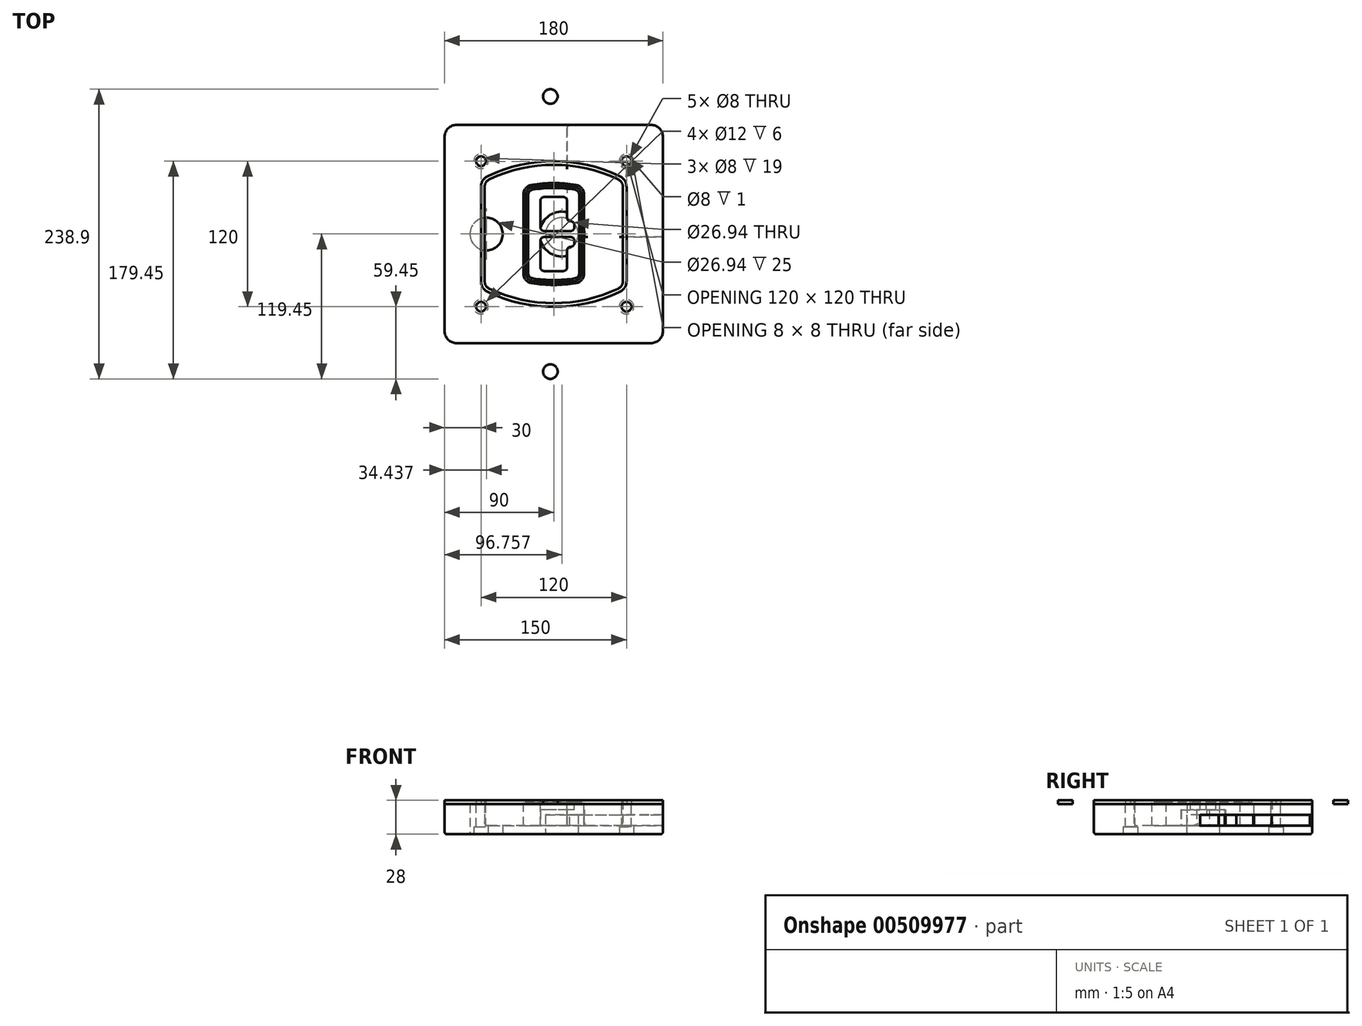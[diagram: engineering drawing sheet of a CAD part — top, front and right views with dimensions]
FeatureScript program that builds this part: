
annotation { "Feature Type Name" : "Feature", "Feature Type Description" : "" }
export const myFeature = defineFeature(function(context is Context, id is Id, definition is map)
    precondition{}
    {
        {
            var Q0;
            Q0=qCreatedBy(makeId("Top.planeOp"),FACE);
            var sketch = newSketch(context, id + "F0", { "sketchPlane" : qUnion([Q0])});
            skPoint(sketch, "E0.rect.middle", {"position": v(0, 0) * mm});
            skLineSegment(sketch, "E1.bottom", {"start": v(-80, -90) * mm, "end": v(80, -90) * mm});
            skLineSegment(sketch, "E1.top", {"start": v(-80, 90) * mm, "end": v(80, 90) * mm});
            skLineSegment(sketch, "E1.left", {"start": v(-90, -80) * mm, "end": v(-90, 80) * mm});
            skLineSegment(sketch, "E1.right", {"start": v(90, -80) * mm, "end": v(90, 80) * mm});
            skLineSegment(sketch, "E2", {"start": v(-90, 90) * mm, "end": v(90, -90) * mm, "construction": true});
            skLineSegment(sketch, "E3", {"start": v(90, 90) * mm, "end": v(-90, -90) * mm, "construction": true});
            skCircle(sketch, "E4", {"center": v(-60, 60) * mm, "radius": 4 * mm});
            skCircle(sketch, "E5", {"center": v(60, 60) * mm, "radius": 4 * mm});
            skCircle(sketch, "E6", {"center": v(60, -60) * mm, "radius": 4 * mm});
            skCircle(sketch, "E7", {"center": v(-60, -60) * mm, "radius": 4 * mm});
            skLineSegment(sketch, "E8", {"start": v(-60, 60) * mm, "end": v(60, 60) * mm, "construction": true});
            skLineSegment(sketch, "E9", {"start": v(60, 60) * mm, "end": v(60, -60) * mm, "construction": true});
            skLineSegment(sketch, "E10", {"start": v(60, -60) * mm, "end": v(-60, -60) * mm, "construction": true});
            skLineSegment(sketch, "E11", {"start": v(-60, -60) * mm, "end": v(-60, 60) * mm, "construction": true});
            skLineSegment(sketch, "E12", {"start": v(-60, 38.83) * mm, "end": v(-60, -38.83) * mm});
            skLineSegment(sketch, "E13", {"start": v(60, 38.83) * mm, "end": v(60, -38.83) * mm});
            skArc(sketch, "E14", {"start": v(54.26, 47.88) * mm, "mid": v(0, 60) * mm, "end": v(-54.26, 47.88) * mm});
            skArc(sketch, "E15", {"start": v(-54.26, -47.88) * mm, "mid": v(0, -60) * mm, "end": v(54.26, -47.88) * mm});
            skLineSegment(sketch, "E16", {"start": v(-60, 0) * mm, "end": v(60, 0) * mm, "construction": true});
            skPoint(sketch, "E17.visualSharp", {"position": v(-60, -45) * mm});
            skArc(sketch, "E17.filletArc", {"start": v(-60, -38.83) * mm, "mid": v(-58.44, -44.2) * mm, "end": v(-54.26, -47.88) * mm});
            skPoint(sketch, "E18.visualSharp", {"position": v(-60, 45) * mm});
            skArc(sketch, "E18.filletArc", {"start": v(-54.26, 47.88) * mm, "mid": v(-58.44, 44.2) * mm, "end": v(-60, 38.83) * mm});
            skPoint(sketch, "E19.visualSharp", {"position": v(60, 45) * mm});
            skArc(sketch, "E19.filletArc", {"start": v(60, 38.83) * mm, "mid": v(58.44, 44.2) * mm, "end": v(54.26, 47.88) * mm});
            skPoint(sketch, "E20.visualSharp", {"position": v(60, -45) * mm});
            skArc(sketch, "E20.filletArc", {"start": v(54.26, -47.88) * mm, "mid": v(58.44, -44.2) * mm, "end": v(60, -38.83) * mm});
            skPoint(sketch, "E21.visualSharp", {"position": v(-90, 90) * mm});
            skArc(sketch, "E21.filletArc", {"start": v(-80, 90) * mm, "mid": v(-87.07, 87.07) * mm, "end": v(-90, 80) * mm});
            skPoint(sketch, "E22.visualSharp", {"position": v(90, 90) * mm});
            skArc(sketch, "E22.filletArc", {"start": v(90, 80) * mm, "mid": v(87.07, 87.07) * mm, "end": v(80, 90) * mm});
            skPoint(sketch, "E23.visualSharp", {"position": v(90, -90) * mm});
            skArc(sketch, "E23.filletArc", {"start": v(80, -90) * mm, "mid": v(87.07, -87.07) * mm, "end": v(90, -80) * mm});
            skPoint(sketch, "E24.visualSharp", {"position": v(-90, -90) * mm});
            skArc(sketch, "E24.filletArc", {"start": v(-90, -80) * mm, "mid": v(-87.07, -87.07) * mm, "end": v(-80, -90) * mm});
            skArc(sketch, "E25.0", {"start": v(57, 38.83) * mm, "mid": v(55.9, 42.58) * mm, "end": v(52.98, 45.17) * mm});
            skLineSegment(sketch, "E25.1", {"start": v(57, 38.83) * mm, "end": v(57, -38.83) * mm});
            skArc(sketch, "E25.2", {"start": v(52.98, -45.17) * mm, "mid": v(55.9, -42.58) * mm, "end": v(57, -38.83) * mm});
            skArc(sketch, "E25.3", {"start": v(-52.98, -45.17) * mm, "mid": v(0, -57) * mm, "end": v(52.98, -45.17) * mm});
            skArc(sketch, "E25.4", {"start": v(-57, -38.83) * mm, "mid": v(-55.9, -42.58) * mm, "end": v(-52.98, -45.17) * mm});
            skArc(sketch, "E25.5", {"start": v(52.98, 45.17) * mm, "mid": v(0, 57) * mm, "end": v(-52.98, 45.17) * mm});
            skLineSegment(sketch, "E25.6", {"start": v(-57, 38.83) * mm, "end": v(-57, -38.83) * mm});
            skArc(sketch, "E25.7", {"start": v(-52.98, 45.17) * mm, "mid": v(-55.9, 42.58) * mm, "end": v(-57, 38.83) * mm});
            skArc(sketch, "E26.0", {"start": v(-55.96, 51.5) * mm, "mid": v(-61.82, 46.33) * mm, "end": v(-64, 38.83) * mm});
            skArc(sketch, "E26.1", {"start": v(55.96, 51.5) * mm, "mid": v(0, 64) * mm, "end": v(-55.96, 51.5) * mm});
            skArc(sketch, "E26.2", {"start": v(64, 38.83) * mm, "mid": v(61.82, 46.33) * mm, "end": v(55.96, 51.5) * mm});
            skLineSegment(sketch, "E26.3", {"start": v(64, 38.83) * mm, "end": v(64, -38.83) * mm});
            skArc(sketch, "E26.4", {"start": v(55.96, -51.5) * mm, "mid": v(61.82, -46.33) * mm, "end": v(64, -38.83) * mm});
            skLineSegment(sketch, "E26.5", {"start": v(-64, 38.83) * mm, "end": v(-64, -38.83) * mm});
            skArc(sketch, "E26.6", {"start": v(-55.96, -51.5) * mm, "mid": v(0, -64) * mm, "end": v(55.96, -51.5) * mm});
            skArc(sketch, "E26.7", {"start": v(-64, -38.83) * mm, "mid": v(-61.82, -46.33) * mm, "end": v(-55.96, -51.5) * mm});
            skSolve(sketch);
        }
        {
            var Q0;
            Q0=makeQuery(id+"F0.imprint","IMPRINT",FACE,{"disambiguationData":[TD([[makeQuery(id+"F0.imprint","IMPRINT",EDGE,{"derivedFrom":sQuery(id+"F0.wireOp",EDGE,"E1.bottom")}),1.0]])]});
            var Q1;
            Q1=makeQuery(id+"F0.imprint","IMPRINT",FACE,{"disambiguationData":[TD([[makeQuery(id+"F0.imprint","IMPRINT",EDGE,{"derivedFrom":sQuery(id+"F0.wireOp",EDGE,"E12")}),1.0]])]});
            var Q2;
            Q2=makeQuery(id+"F0.imprint","IMPRINT",FACE,{"disambiguationData":[TD([[makeQuery(id+"F0.imprint","IMPRINT",EDGE,{"derivedFrom":sQuery(id+"F0.wireOp",EDGE,"E25.0")}),1.0]])]});
            var Q3;
            Q3=makeQuery(id+"F0.imprint","IMPRINT",FACE,{"disambiguationData":[TD([[makeQuery(id+"F0.imprint","IMPRINT",EDGE,{"derivedFrom":sQuery(id+"F0.wireOp",EDGE,"E12")}),-1.0]])]});
            extrude(context, id + "F1", {"entities" : qUnion([Q0, Q1, Q2, Q3]), "oppositeDirection" : true, "depth" : 25 * mm});
        }
        {
            var Q0;
            Q0=makeQuery(id+"F0.imprint","IMPRINT",FACE,{"disambiguationData":[TD([[makeQuery(id+"F0.imprint","IMPRINT",EDGE,{"derivedFrom":sQuery(id+"F0.wireOp",EDGE,"E12")}),1.0]])]});
            extrude(context, id + "F2", {"entities" : qUnion([Q0]), "operationType" : NewBodyOperationType.ADD, "depth" : 3 * mm});
        }
        {
            var Q0;
            Q0=makeQuery(id+"F0.imprint","IMPRINT",FACE,{"disambiguationData":[TD([[makeQuery(id+"F0.imprint","IMPRINT",EDGE,{"derivedFrom":sQuery(id+"F0.wireOp",EDGE,"E25.0")}),1.0]])]});
            extrude(context, id + "F3", {"entities" : qUnion([Q0]), "operationType" : NewBodyOperationType.REMOVE, "oppositeDirection" : true, "depth" : 18 * mm});
        }
        {
            var Q0;
            Q0=makeQuery(id+"F2.opExtrude","CAP_FACE",FACE,{"disambiguationData":[OSD([sQuery(id+"F0.wireOp",EDGE,"E12"),sQuery(id+"F0.wireOp",EDGE,"E13"),sQuery(id+"F0.wireOp",EDGE,"E14"),sQuery(id+"F0.wireOp",EDGE,"E15"),sQuery(id+"F0.wireOp",EDGE,"E17.filletArc"),sQuery(id+"F0.wireOp",EDGE,"E18.filletArc"),sQuery(id+"F0.wireOp",EDGE,"E19.filletArc"),sQuery(id+"F0.wireOp",EDGE,"E20.filletArc"),sQuery(id+"F0.wireOp",EDGE,"E25.0"),sQuery(id+"F0.wireOp",EDGE,"E25.1"),sQuery(id+"F0.wireOp",EDGE,"E25.2"),sQuery(id+"F0.wireOp",EDGE,"E25.3"),sQuery(id+"F0.wireOp",EDGE,"E25.4"),sQuery(id+"F0.wireOp",EDGE,"E25.5"),sQuery(id+"F0.wireOp",EDGE,"E25.6"),sQuery(id+"F0.wireOp",EDGE,"E25.7")])],"isStart":false});
            var sketch = newSketch(context, id + "F4", { "sketchPlane" : qUnion([Q0])});
            skArc(sketch, "E27.0", {"start": v(-18.34, -40.45) * mm, "mid": v(0, -42) * mm, "end": v(18.34, -40.45) * mm});
            skArc(sketch, "E28.0", {"start": v(18.34, 40.45) * mm, "mid": v(0, 42) * mm, "end": v(-18.34, 40.45) * mm});
            skLineSegment(sketch, "E29", {"start": v(-25, 32.57) * mm, "end": v(-25, -32.57) * mm});
            skLineSegment(sketch, "E30", {"start": v(25, 32.57) * mm, "end": v(25, -32.57) * mm});
            skLineSegment(sketch, "E31", {"start": v(-25, 39.1) * mm, "end": v(25, 39.1) * mm, "construction": true});
            skLineSegment(sketch, "E32", {"start": v(-25, -39.1) * mm, "end": v(25, -39.1) * mm, "construction": true});
            skPoint(sketch, "E33.visualSharp", {"position": v(-25, 39.1) * mm});
            skArc(sketch, "E33.filletArc", {"start": v(-18.34, 40.45) * mm, "mid": v(-23.11, 37.73) * mm, "end": v(-25, 32.57) * mm});
            skPoint(sketch, "E34.visualSharp", {"position": v(25, 39.1) * mm});
            skArc(sketch, "E34.filletArc", {"start": v(25, 32.57) * mm, "mid": v(23.11, 37.73) * mm, "end": v(18.34, 40.45) * mm});
            skPoint(sketch, "E35.visualSharp", {"position": v(25, -39.1) * mm});
            skArc(sketch, "E35.filletArc", {"start": v(18.34, -40.45) * mm, "mid": v(23.11, -37.73) * mm, "end": v(25, -32.57) * mm});
            skPoint(sketch, "E36.visualSharp", {"position": v(-25, -39.1) * mm});
            skArc(sketch, "E36.filletArc", {"start": v(-25, -32.57) * mm, "mid": v(-23.11, -37.73) * mm, "end": v(-18.34, -40.45) * mm});
            skArc(sketch, "E37.0", {"start": v(52.98, 45.17) * mm, "mid": v(0, 57) * mm, "end": v(-52.98, 45.17) * mm});
            skArc(sketch, "E37.1", {"start": v(-52.98, 45.17) * mm, "mid": v(-55.9, 42.58) * mm, "end": v(-57, 38.83) * mm});
            skLineSegment(sketch, "E37.2", {"start": v(-57, 38.83) * mm, "end": v(-57, -38.83) * mm});
            skArc(sketch, "E37.3", {"start": v(-57, -38.83) * mm, "mid": v(-55.9, -42.58) * mm, "end": v(-52.98, -45.17) * mm});
            skArc(sketch, "E37.4", {"start": v(-52.98, -45.17) * mm, "mid": v(0, -57) * mm, "end": v(52.98, -45.17) * mm});
            skArc(sketch, "E37.5", {"start": v(52.98, -45.17) * mm, "mid": v(55.9, -42.58) * mm, "end": v(57, -38.83) * mm});
            skLineSegment(sketch, "E37.6", {"start": v(57, 38.83) * mm, "end": v(57, -38.83) * mm});
            skArc(sketch, "E37.7", {"start": v(57, 38.83) * mm, "mid": v(55.9, 42.58) * mm, "end": v(52.98, 45.17) * mm});
            skLineSegment(sketch, "E38.0", {"start": v(23, 32.57) * mm, "end": v(23, -32.57) * mm});
            skArc(sketch, "E38.1", {"start": v(18, -38.48) * mm, "mid": v(21.58, -36.44) * mm, "end": v(23, -32.57) * mm});
            skArc(sketch, "E38.2", {"start": v(-18, -38.48) * mm, "mid": v(0, -40) * mm, "end": v(18, -38.48) * mm});
            skArc(sketch, "E38.3", {"start": v(-23, -32.57) * mm, "mid": v(-21.58, -36.44) * mm, "end": v(-18, -38.48) * mm});
            skLineSegment(sketch, "E38.4", {"start": v(-23, 32.57) * mm, "end": v(-23, -32.57) * mm});
            skArc(sketch, "E38.5", {"start": v(23, 32.57) * mm, "mid": v(21.58, 36.44) * mm, "end": v(18, 38.48) * mm});
            skArc(sketch, "E38.6", {"start": v(-18, 38.48) * mm, "mid": v(-21.58, 36.44) * mm, "end": v(-23, 32.57) * mm});
            skArc(sketch, "E38.7", {"start": v(18, 38.48) * mm, "mid": v(0, 40) * mm, "end": v(-18, 38.48) * mm});
            skArc(sketch, "E39.0", {"start": v(21, 32.57) * mm, "mid": v(20.06, 35.15) * mm, "end": v(17.67, 36.5) * mm});
            skLineSegment(sketch, "E39.1", {"start": v(21, 32.57) * mm, "end": v(21, -32.57) * mm});
            skArc(sketch, "E39.2", {"start": v(17.67, -36.5) * mm, "mid": v(20.06, -35.15) * mm, "end": v(21, -32.57) * mm});
            skArc(sketch, "E39.3", {"start": v(-17.67, -36.5) * mm, "mid": v(0, -38) * mm, "end": v(17.67, -36.5) * mm});
            skArc(sketch, "E39.4", {"start": v(-21, -32.57) * mm, "mid": v(-20.06, -35.15) * mm, "end": v(-17.67, -36.5) * mm});
            skArc(sketch, "E39.5", {"start": v(17.67, 36.5) * mm, "mid": v(0, 38) * mm, "end": v(-17.67, 36.5) * mm});
            skLineSegment(sketch, "E39.6", {"start": v(-21, 32.57) * mm, "end": v(-21, -32.57) * mm});
            skArc(sketch, "E39.7", {"start": v(-17.67, 36.5) * mm, "mid": v(-20.06, 35.15) * mm, "end": v(-21, 32.57) * mm});
            skLineSegment(sketch, "E40", {"start": v(-25, 0) * mm, "end": v(25, 0) * mm, "construction": true});
            skLineSegment(sketch, "E41", {"start": v(-11, 5.5) * mm, "end": v(-11, 27.5) * mm});
            skLineSegment(sketch, "E42", {"start": v(-8, 30.5) * mm, "end": v(8, 30.5) * mm});
            skLineSegment(sketch, "E43", {"start": v(11, 27.5) * mm, "end": v(11, 13.5) * mm});
            skLineSegment(sketch, "E44", {"start": v(14, 10.5) * mm, "end": v(14, 10.5) * mm});
            skLineSegment(sketch, "E45", {"start": v(17, 7.5) * mm, "end": v(17, 5.5) * mm});
            skLineSegment(sketch, "E46", {"start": v(14, 2.5) * mm, "end": v(-8, 2.5) * mm});
            skPoint(sketch, "E47.visualSharp", {"position": v(-11, 30.5) * mm});
            skArc(sketch, "E47.filletArc", {"start": v(-8, 30.5) * mm, "mid": v(-10.12, 29.62) * mm, "end": v(-11, 27.5) * mm});
            skPoint(sketch, "E48.visualSharp", {"position": v(11, 30.5) * mm});
            skArc(sketch, "E48.filletArc", {"start": v(11, 27.5) * mm, "mid": v(10.12, 29.62) * mm, "end": v(8, 30.5) * mm});
            skPoint(sketch, "E49.visualSharp", {"position": v(11, 10.5) * mm});
            skArc(sketch, "E49.filletArc", {"start": v(11, 13.5) * mm, "mid": v(11.88, 11.38) * mm, "end": v(14, 10.5) * mm});
            skPoint(sketch, "E50.visualSharp", {"position": v(17, 10.5) * mm});
            skArc(sketch, "E50.filletArc", {"start": v(17, 7.5) * mm, "mid": v(16.12, 9.62) * mm, "end": v(14, 10.5) * mm});
            skPoint(sketch, "E51.visualSharp", {"position": v(17, 2.5) * mm});
            skArc(sketch, "E51.filletArc", {"start": v(14, 2.5) * mm, "mid": v(16.12, 3.38) * mm, "end": v(17, 5.5) * mm});
            skPoint(sketch, "E52.visualSharp", {"position": v(-11, 2.5) * mm});
            skArc(sketch, "E52.filletArc", {"start": v(-11, 5.5) * mm, "mid": v(-10.12, 3.38) * mm, "end": v(-8, 2.5) * mm});
            skLineSegment(sketch, "E53.0.MirrorCS", {"start": v(14, -2.5) * mm, "end": v(-8, -2.5) * mm});
            skArc(sketch, "E54.0.MirrorCS", {"start": v(-11, -5.5) * mm, "mid": v(-10.12, -3.38) * mm, "end": v(-8, -2.5) * mm});
            skLineSegment(sketch, "E55.0.MirrorCS", {"start": v(-11, -5.5) * mm, "end": v(-11, -27.5) * mm});
            skArc(sketch, "E56.0.MirrorCS", {"start": v(-8, -30.5) * mm, "mid": v(-10.12, -29.62) * mm, "end": v(-11, -27.5) * mm});
            skLineSegment(sketch, "E57.0.MirrorCS", {"start": v(-8, -30.5) * mm, "end": v(8, -30.5) * mm});
            skArc(sketch, "E58.0.MirrorCS", {"start": v(11, -27.5) * mm, "mid": v(10.12, -29.62) * mm, "end": v(8, -30.5) * mm});
            skLineSegment(sketch, "E59.0.MirrorCS", {"start": v(11, -27.5) * mm, "end": v(11, -13.5) * mm});
            skArc(sketch, "E60.0.MirrorCS", {"start": v(11, -13.5) * mm, "mid": v(11.88, -11.38) * mm, "end": v(14, -10.5) * mm});
            skArc(sketch, "E61.0.MirrorCS", {"start": v(17, -7.5) * mm, "mid": v(16.12, -9.62) * mm, "end": v(14, -10.5) * mm});
            skLineSegment(sketch, "E62.0.MirrorCS", {"start": v(17, -7.5) * mm, "end": v(17, -5.5) * mm});
            skArc(sketch, "E63.0.MirrorCS", {"start": v(14, -2.5) * mm, "mid": v(16.12, -3.38) * mm, "end": v(17, -5.5) * mm});
            skSolve(sketch);
        }
        {
            var Q0;
            Q0=makeQuery(id+"F4.imprint","IMPRINT",FACE,{"disambiguationData":[TD([[makeQuery(id+"F4.imprint","IMPRINT",EDGE,{"derivedFrom":sQuery(id+"F4.wireOp",EDGE,"E27.0")}),1.0]])]});
            var Q1;
            Q1=makeQuery(id+"F4.imprint","IMPRINT",FACE,{"disambiguationData":[TD([[makeQuery(id+"F4.imprint","IMPRINT",EDGE,{"derivedFrom":sQuery(id+"F4.wireOp",EDGE,"E38.0")}),-1.0]])]});
            var Q2;
            Q2=makeQuery(id+"F4.imprint","IMPRINT",FACE,{"disambiguationData":[TD([[makeQuery(id+"F4.imprint","IMPRINT",EDGE,{"derivedFrom":sQuery(id+"F4.wireOp",EDGE,"E39.0")}),1.0]])]});
            extrude(context, id + "F5", {"entities" : qUnion([Q0, Q1, Q2]), "operationType" : NewBodyOperationType.ADD, "endBound" : BoundingType.UP_TO_NEXT, "oppositeDirection" : true, "depth" : 25 * mm});
        }
        {
            var Q0;
            Q0=makeQuery(id+"F4.imprint","IMPRINT",FACE,{"disambiguationData":[TD([[makeQuery(id+"F4.imprint","IMPRINT",EDGE,{"derivedFrom":sQuery(id+"F4.wireOp",EDGE,"E38.0")}),-1.0]])]});
            extrude(context, id + "F6", {"entities" : qUnion([Q0]), "operationType" : NewBodyOperationType.REMOVE, "oppositeDirection" : true, "depth" : 2 * mm});
        }
        {
            var Q0;
            Q0=makeQuery(id+"F1.opExtrude","CAP_FACE",FACE,{"disambiguationData":[OSD([sQuery(id+"F0.wireOp",EDGE,"E1.bottom"),sQuery(id+"F0.wireOp",EDGE,"E1.top"),sQuery(id+"F0.wireOp",EDGE,"E1.left"),sQuery(id+"F0.wireOp",EDGE,"E1.right"),sQuery(id+"F0.wireOp",EDGE,"E4"),sQuery(id+"F0.wireOp",EDGE,"E5"),sQuery(id+"F0.wireOp",EDGE,"E6"),sQuery(id+"F0.wireOp",EDGE,"E7"),sQuery(id+"F0.wireOp",EDGE,"E21.filletArc"),sQuery(id+"F0.wireOp",EDGE,"E22.filletArc"),sQuery(id+"F0.wireOp",EDGE,"E23.filletArc"),sQuery(id+"F0.wireOp",EDGE,"E24.filletArc")])],"isStart":false});
            var sketch = newSketch(context, id + "F7", { "sketchPlane" : qUnion([Q0])});
            skCircle(sketch, "E64", {"center": v(6.76, 0) * mm, "radius": 13.47 * mm});
            skCircle(sketch, "E65", {"center": v(-55.56, 0) * mm, "radius": 13.47 * mm});
            skLineSegment(sketch, "E66", {"start": v(90, 0) * mm, "end": v(-90, 0) * mm});
            skCircle(sketch, "E67", {"center": v(6.76, 0) * mm, "radius": 18.47 * mm});
            skCircle(sketch, "E68", {"center": v(60, -60) * mm, "radius": 6 * mm});
            skCircle(sketch, "E69", {"center": v(-60, -60) * mm, "radius": 6 * mm});
            skCircle(sketch, "E70", {"center": v(-60, 60) * mm, "radius": 6 * mm});
            skCircle(sketch, "E71", {"center": v(60, 60) * mm, "radius": 6 * mm});
            skSolve(sketch);
        }
        {
            var Q0;
            {var subQ1=sQuery(id+"F7.wireOp",EDGE,"E66");var subQ4=sQuery(id+"F7.wireOp",EDGE,"E64");var subQ6=makeQuery(id+"F7.imprint","INTERSECT",VERTEX,{"disambiguationData":[OD(0.0)],"derivedFrom":[subQ4,subQ1]});Q0=makeQuery(id+"F7.imprint","IMPRINT",FACE,{"disambiguationData":[TD([[makeQuery(id+"F7.imprint","IMPRINT",EDGE,{"disambiguationData":[TD([[subQ6,-1.0]])],"derivedFrom":subQ4}),-1.0]])]});}
            var Q1;
            {var subQ0=sQuery(id+"F7.wireOp",EDGE,"E66");var subQ1=sQuery(id+"F7.wireOp",EDGE,"E64");var subQ3=makeQuery(id+"F7.imprint","INTERSECT",VERTEX,{"disambiguationData":[OD(0.0)],"derivedFrom":[subQ1,subQ0]});Q1=makeQuery(id+"F7.imprint","IMPRINT",FACE,{"disambiguationData":[TD([[makeQuery(id+"F7.imprint","IMPRINT",EDGE,{"disambiguationData":[TD([[subQ3,-1.0]])],"derivedFrom":subQ1}),1.0]])]});}
            var Q2;
            {var subQ0=sQuery(id+"F7.wireOp",EDGE,"E66");var subQ1=sQuery(id+"F7.wireOp",EDGE,"E64");var subQ3=makeQuery(id+"F7.imprint","INTERSECT",VERTEX,{"disambiguationData":[OD(0.0)],"derivedFrom":[subQ1,subQ0]});Q2=makeQuery(id+"F7.imprint","IMPRINT",FACE,{"disambiguationData":[TD([[makeQuery(id+"F7.imprint","IMPRINT",EDGE,{"disambiguationData":[TD([[subQ3,1.0]])],"derivedFrom":subQ1}),1.0]])]});}
            var Q3;
            {var subQ1=sQuery(id+"F7.wireOp",EDGE,"E66");var subQ4=sQuery(id+"F7.wireOp",EDGE,"E64");var subQ6=makeQuery(id+"F7.imprint","INTERSECT",VERTEX,{"disambiguationData":[OD(0.0)],"derivedFrom":[subQ4,subQ1]});Q3=makeQuery(id+"F7.imprint","IMPRINT",FACE,{"disambiguationData":[TD([[makeQuery(id+"F7.imprint","IMPRINT",EDGE,{"disambiguationData":[TD([[subQ6,1.0]])],"derivedFrom":subQ4}),-1.0]])]});}
            extrude(context, id + "F8", {"entities" : qUnion([Q0, Q1, Q2, Q3]), "operationType" : NewBodyOperationType.ADD, "oppositeDirection" : true, "depth" : 20 * mm});
        }
        {
            var Q0;
            {var subQ0=sQuery(id+"F7.wireOp",EDGE,"E66");var subQ1=sQuery(id+"F7.wireOp",EDGE,"E64");var subQ3=makeQuery(id+"F7.imprint","INTERSECT",VERTEX,{"disambiguationData":[OD(0.0)],"derivedFrom":[subQ1,subQ0]});Q0=makeQuery(id+"F7.imprint","IMPRINT",FACE,{"disambiguationData":[TD([[makeQuery(id+"F7.imprint","IMPRINT",EDGE,{"disambiguationData":[TD([[subQ3,-1.0]])],"derivedFrom":subQ1}),1.0]])]});}
            var Q1;
            {var subQ0=sQuery(id+"F7.wireOp",EDGE,"E66");var subQ1=sQuery(id+"F7.wireOp",EDGE,"E64");var subQ3=makeQuery(id+"F7.imprint","INTERSECT",VERTEX,{"disambiguationData":[OD(0.0)],"derivedFrom":[subQ1,subQ0]});Q1=makeQuery(id+"F7.imprint","IMPRINT",FACE,{"disambiguationData":[TD([[makeQuery(id+"F7.imprint","IMPRINT",EDGE,{"disambiguationData":[TD([[subQ3,1.0]])],"derivedFrom":subQ1}),1.0]])]});}
            extrude(context, id + "F9", {"entities" : qUnion([Q0, Q1]), "operationType" : NewBodyOperationType.REMOVE, "oppositeDirection" : true, "depth" : 16 * mm});
        }
        {
            var Q0;
            {var subQ0=sQuery(id+"F7.wireOp",EDGE,"E66");var subQ1=sQuery(id+"F7.wireOp",EDGE,"E65");var subQ3=makeQuery(id+"F7.imprint","INTERSECT",VERTEX,{"disambiguationData":[OD(0.0)],"derivedFrom":[subQ1,subQ0]});Q0=makeQuery(id+"F7.imprint","IMPRINT",FACE,{"disambiguationData":[TD([[makeQuery(id+"F7.imprint","IMPRINT",EDGE,{"disambiguationData":[TD([[subQ3,-1.0]])],"derivedFrom":subQ1}),1.0]])]});}
            var Q1;
            {var subQ0=sQuery(id+"F7.wireOp",EDGE,"E66");var subQ1=sQuery(id+"F7.wireOp",EDGE,"E65");var subQ3=makeQuery(id+"F7.imprint","INTERSECT",VERTEX,{"disambiguationData":[OD(0.0)],"derivedFrom":[subQ1,subQ0]});Q1=makeQuery(id+"F7.imprint","IMPRINT",FACE,{"disambiguationData":[TD([[makeQuery(id+"F7.imprint","IMPRINT",EDGE,{"disambiguationData":[TD([[subQ3,1.0]])],"derivedFrom":subQ1}),1.0]])]});}
            extrude(context, id + "F10", {"entities" : qUnion([Q0, Q1]), "operationType" : NewBodyOperationType.REMOVE, "oppositeDirection" : true, "depth" : 25 * mm});
        }
        {
            var Q0;
            Q0=makeQuery(id+"F7.imprint","IMPRINT",FACE,{"disambiguationData":[TD([[makeQuery(id+"F7.imprint","IMPRINT",EDGE,{"derivedFrom":sQuery(id+"F7.wireOp",EDGE,"E68")}),1.0]])]});
            var Q1;
            Q1=makeQuery(id+"F7.imprint","IMPRINT",FACE,{"disambiguationData":[TD([[makeQuery(id+"F7.imprint","IMPRINT",EDGE,{"derivedFrom":makeQuery(id+"F1.opExtrude","CAP_EDGE",EDGE,{"disambiguationData":[OSD([sQuery(id+"F0.wireOp",EDGE,"E5")])],"isStart":false})}),-1.0]])]});
            var Q2;
            Q2=makeQuery(id+"F7.imprint","IMPRINT",FACE,{"disambiguationData":[TD([[makeQuery(id+"F7.imprint","IMPRINT",EDGE,{"derivedFrom":sQuery(id+"F7.wireOp",EDGE,"E69")}),1.0]])]});
            var Q3;
            Q3=makeQuery(id+"F7.imprint","IMPRINT",FACE,{"disambiguationData":[TD([[makeQuery(id+"F7.imprint","IMPRINT",EDGE,{"derivedFrom":makeQuery(id+"F1.opExtrude","CAP_EDGE",EDGE,{"disambiguationData":[OSD([sQuery(id+"F0.wireOp",EDGE,"E4")])],"isStart":false})}),-1.0]])]});
            var Q4;
            Q4=makeQuery(id+"F7.imprint","IMPRINT",FACE,{"disambiguationData":[TD([[makeQuery(id+"F7.imprint","IMPRINT",EDGE,{"derivedFrom":sQuery(id+"F7.wireOp",EDGE,"E70")}),1.0]])]});
            var Q5;
            Q5=makeQuery(id+"F7.imprint","IMPRINT",FACE,{"disambiguationData":[TD([[makeQuery(id+"F7.imprint","IMPRINT",EDGE,{"derivedFrom":makeQuery(id+"F1.opExtrude","CAP_EDGE",EDGE,{"disambiguationData":[OSD([sQuery(id+"F0.wireOp",EDGE,"E7")])],"isStart":false})}),-1.0]])]});
            var Q6;
            Q6=makeQuery(id+"F7.imprint","IMPRINT",FACE,{"disambiguationData":[TD([[makeQuery(id+"F7.imprint","IMPRINT",EDGE,{"derivedFrom":sQuery(id+"F7.wireOp",EDGE,"E71")}),1.0]])]});
            var Q7;
            Q7=makeQuery(id+"F7.imprint","IMPRINT",FACE,{"disambiguationData":[TD([[makeQuery(id+"F7.imprint","IMPRINT",EDGE,{"derivedFrom":makeQuery(id+"F1.opExtrude","CAP_EDGE",EDGE,{"disambiguationData":[OSD([sQuery(id+"F0.wireOp",EDGE,"E6")])],"isStart":false})}),-1.0]])]});
            extrude(context, id + "F11", {"entities" : qUnion([Q0, Q1, Q2, Q3, Q4, Q5, Q6, Q7]), "operationType" : NewBodyOperationType.REMOVE, "oppositeDirection" : true, "depth" : 6 * mm});
        }
        {
            var Q0;
            Q0=makeQuery(id+"F9.boolean.opBoolean","COPY",FACE,{"derivedFrom":makeQuery(id+"F9.opExtrude","CAP_FACE",FACE,{"disambiguationData":[OSD([sQuery(id+"F7.wireOp",EDGE,"E64")])],"isStart":false})});
            var sketch = newSketch(context, id + "F12", { "sketchPlane" : qUnion([Q0])});
            skArc(sketch, "E72.0", {"start": v(11, -88.19) * mm, "mid": v(97.1, -83.6) * mm, "end": v(92.5, 2.5) * mm});
            skLineSegment(sketch, "E72.1", {"start": v(11, -17.97) * mm, "end": v(11, -17.97) * mm});
            skLineSegment(sketch, "E73", {"start": v(92.5, -105.13) * mm, "end": v(102.3, -105.13) * mm});
            skLineSegment(sketch, "E74.0", {"start": v(92.5, 2.5) * mm, "end": v(14, 2.5) * mm});
            skArc(sketch, "E74.1", {"start": v(14, 2.5) * mm, "mid": v(16.12, 3.38) * mm, "end": v(17, 5.5) * mm});
            skLineSegment(sketch, "E74.2", {"start": v(17, 7.5) * mm, "end": v(17, 5.5) * mm});
            skArc(sketch, "E74.3", {"start": v(17, 7.5) * mm, "mid": v(16.12, 9.62) * mm, "end": v(14, 10.5) * mm});
            skArc(sketch, "E74.4", {"start": v(11, 13.5) * mm, "mid": v(11.88, 11.38) * mm, "end": v(14, 10.5) * mm});
            skLineSegment(sketch, "E74.5", {"start": v(11, 13.5) * mm, "end": v(11, -88.19) * mm});
            skLineSegment(sketch, "E74.7", {"start": v(92.5, -2.5) * mm, "end": v(14, -2.5) * mm});
            skArc(sketch, "E74.8", {"start": v(14, -2.5) * mm, "mid": v(16.12, -3.38) * mm, "end": v(17, -5.5) * mm});
            skLineSegment(sketch, "E74.9", {"start": v(17, -7.5) * mm, "end": v(17, -5.5) * mm});
            skArc(sketch, "E74.10", {"start": v(17, -7.5) * mm, "mid": v(16.12, -9.62) * mm, "end": v(14, -10.5) * mm});
            skArc(sketch, "E74.11", {"start": v(11, -13.5) * mm, "mid": v(11.88, -11.38) * mm, "end": v(14, -10.5) * mm});
            skLineSegment(sketch, "E74.12", {"start": v(11, -17.97) * mm, "end": v(11, -13.5) * mm});
            skPoint(sketch, "E75.orphan", {"position": v(11, -27.5) * mm});
            skPoint(sketch, "E76.orphan", {"position": v(-8, -2.5) * mm});
            skPoint(sketch, "E77.orphan", {"position": v(-8, 2.5) * mm});
            skPoint(sketch, "E78.orphan", {"position": v(11, 27.5) * mm});
            skSolve(sketch);
        }
        {
            var Q0;
            {var subQ7=sQuery(id+"F12.wireOp",EDGE,"E72.0");var subQ14=sQuery(id+"F12.wireOp",EDGE,"E72.1");var subQ16=sQuery(id+"F12.wireOp",EDGE,"E74.1");var subQ18=sQuery(id+"F12.wireOp",EDGE,"E74.8");Q0=qUnion([makeQuery(id+"F12.imprint","IMPRINT",FACE,{"disambiguationData":[TD([[makeQuery(id+"F12.imprint","IMPRINT",EDGE,{"derivedFrom":subQ7}),1.0]])]}),makeQuery(id+"F12.imprint","IMPRINT",FACE,{"disambiguationData":[TD([[makeQuery(id+"F12.imprint","IMPRINT",EDGE,{"derivedFrom":subQ14}),1.0]])]}),makeQuery(id+"F12.imprint","IMPRINT",FACE,{"disambiguationData":[TD([[makeQuery(id+"F12.imprint","IMPRINT",EDGE,{"derivedFrom":subQ16}),1.0]])]}),makeQuery(id+"F12.imprint","IMPRINT",FACE,{"disambiguationData":[TD([[makeQuery(id+"F12.imprint","IMPRINT",EDGE,{"derivedFrom":subQ18}),-1.0]])]})]);}
            var Q1;
            Q1=makeQuery(id+"F5.boolean.opBoolean","SPLIT",FACE,{"disambiguationData":[TD([makeQuery(id+"F5.opExtrude","SWEPT_FACE",FACE,{"disambiguationData":[OSD([sQuery(id+"F4.wireOp",EDGE,"E41")])]})])],"derivedFrom":makeQuery(id+"F3.boolean.opBoolean","COPY",FACE,{"derivedFrom":makeQuery(id+"F3.opExtrude","CAP_FACE",FACE,{"disambiguationData":[OSD([sQuery(id+"F0.wireOp",EDGE,"E25.0"),sQuery(id+"F0.wireOp",EDGE,"E25.1"),sQuery(id+"F0.wireOp",EDGE,"E25.2"),sQuery(id+"F0.wireOp",EDGE,"E25.3"),sQuery(id+"F0.wireOp",EDGE,"E25.4"),sQuery(id+"F0.wireOp",EDGE,"E25.5"),sQuery(id+"F0.wireOp",EDGE,"E25.6"),sQuery(id+"F0.wireOp",EDGE,"E25.7")])],"isStart":false})})});
            extrude(context, id + "F13", {"entities" : qUnion([Q0]), "operationType" : NewBodyOperationType.REMOVE, "endBound" : BoundingType.UP_TO_SURFACE, "endBoundEntityFace" : qUnion([Q1]), "depth" : 25 * mm});
        }
        {
            var Q0;
            Q0=makeQuery(id+"F3.boolean.opBoolean","COPY",EDGE,{"derivedFrom":makeQuery(id+"F3.opExtrude","CAP_EDGE",EDGE,{"disambiguationData":[OSD([sQuery(id+"F0.wireOp",EDGE,"E25.6")])],"isStart":false})});
            var Q1;
            Q1=makeQuery(id+"F8.boolean.opBoolean","INTERSECT",EDGE,{"derivedFrom":[makeQuery(id+"F5.opExtrude","SWEPT_FACE",FACE,{"disambiguationData":[OSD([sQuery(id+"F4.wireOp",EDGE,"E30")])]}),makeQuery(id+"F8.opExtrude","CAP_FACE",FACE,{"disambiguationData":[OSD([sQuery(id+"F7.wireOp",EDGE,"E67")])],"isStart":false})]});
            var Q2;
            Q2=makeQuery(id+"F8.boolean.opBoolean","INTERSECT",EDGE,{"disambiguationData":[OD(1.0)],"derivedFrom":[makeQuery(id+"F5.opExtrude","SWEPT_FACE",FACE,{"disambiguationData":[OSD([sQuery(id+"F4.wireOp",EDGE,"E30")])]}),makeQuery(id+"F8.opExtrude","SWEPT_FACE",FACE,{"disambiguationData":[OSD([sQuery(id+"F7.wireOp",EDGE,"E67")])]})]});
            var Q3;
            {var subQ0=makeQuery(id+"F3.boolean.opBoolean","COPY",FACE,{"derivedFrom":makeQuery(id+"F3.opExtrude","CAP_FACE",FACE,{"disambiguationData":[OSD([sQuery(id+"F0.wireOp",EDGE,"E25.0"),sQuery(id+"F0.wireOp",EDGE,"E25.1"),sQuery(id+"F0.wireOp",EDGE,"E25.2"),sQuery(id+"F0.wireOp",EDGE,"E25.3"),sQuery(id+"F0.wireOp",EDGE,"E25.4"),sQuery(id+"F0.wireOp",EDGE,"E25.5"),sQuery(id+"F0.wireOp",EDGE,"E25.6"),sQuery(id+"F0.wireOp",EDGE,"E25.7")])],"isStart":false})});var subQ1=sQuery(id+"F4.wireOp",EDGE,"E30");Q3=makeQuery(id+"F8.boolean.opBoolean","SPLIT",EDGE,{"disambiguationData":[TD([makeQuery(id+"F5.opExtrude","SWEPT_FACE",FACE,{"disambiguationData":[OSD([sQuery(id+"F4.wireOp",EDGE,"E35.filletArc")])]})])],"derivedFrom":makeQuery(id+"F5.opExtrude","TWEAK_EDGE",EDGE,{"derivedFrom":[subQ0,makeQuery(id+"F4.imprint","IMPRINT",EDGE,{"derivedFrom":subQ1})]})});}
            var Q4;
            {var subQ0=sQuery(id+"F0.wireOp",EDGE,"E25.0");var subQ1=sQuery(id+"F0.wireOp",EDGE,"E25.1");var subQ2=sQuery(id+"F0.wireOp",EDGE,"E25.2");var subQ3=sQuery(id+"F0.wireOp",EDGE,"E25.3");var subQ4=sQuery(id+"F0.wireOp",EDGE,"E25.4");var subQ5=sQuery(id+"F0.wireOp",EDGE,"E25.5");var subQ6=sQuery(id+"F0.wireOp",EDGE,"E25.6");var subQ7=sQuery(id+"F0.wireOp",EDGE,"E25.7");Q4=makeQuery(id+"F8.boolean.opBoolean","INTERSECT",EDGE,{"derivedFrom":[makeQuery(id+"F5.boolean.opBoolean","SPLIT",FACE,{"disambiguationData":[TD([makeQuery(id+"F2.opExtrude","SWEPT_FACE",FACE,{"disambiguationData":[OSD([subQ0])]})])],"derivedFrom":makeQuery(id+"F3.boolean.opBoolean","COPY",FACE,{"derivedFrom":makeQuery(id+"F3.opExtrude","CAP_FACE",FACE,{"disambiguationData":[OSD([subQ0,subQ1,subQ2,subQ3,subQ4,subQ5,subQ6,subQ7])],"isStart":false})})}),makeQuery(id+"F8.opExtrude","SWEPT_FACE",FACE,{"disambiguationData":[OSD([sQuery(id+"F7.wireOp",EDGE,"E67")])]})]});}
            var Q5;
            Q5=makeQuery(id+"F8.boolean.opBoolean","INTERSECT",EDGE,{"disambiguationData":[OD(0.0)],"derivedFrom":[makeQuery(id+"F5.opExtrude","SWEPT_FACE",FACE,{"disambiguationData":[OSD([sQuery(id+"F4.wireOp",EDGE,"E30")])]}),makeQuery(id+"F8.opExtrude","SWEPT_FACE",FACE,{"disambiguationData":[OSD([sQuery(id+"F7.wireOp",EDGE,"E67")])]})]});
            fillet(context, id + "F14", {"entities" : qUnion([Q0, Q1, Q2, Q3, Q4, Q5]), "radius" : 3 * mm, "tangentPropagation" : true, "allowEdgeOverflow" : false});
        }
        {
            var Q0;
            Q0=makeQuery(id+"F1.opExtrude","CAP_EDGE",EDGE,{"disambiguationData":[OSD([sQuery(id+"F0.wireOp",EDGE,"E1.bottom")])],"isStart":false});
            fillet(context, id + "F15", {"entities" : qUnion([Q0]), "radius" : 2 * mm, "tangentPropagation" : true, "allowEdgeOverflow" : false});
        }
        {
            var Q0;
            {var subQ0=sQuery(id+"F0.wireOp",EDGE,"E21.filletArc");var subQ1=sQuery(id+"F0.wireOp",EDGE,"E7");var subQ2=sQuery(id+"F0.wireOp",EDGE,"E6");var subQ3=sQuery(id+"F0.wireOp",EDGE,"E5");var subQ4=sQuery(id+"F0.wireOp",EDGE,"E4");var subQ5=sQuery(id+"F0.wireOp",EDGE,"E22.filletArc");var subQ6=sQuery(id+"F0.wireOp",EDGE,"E1.bottom");var subQ7=sQuery(id+"F0.wireOp",EDGE,"E1.right");var subQ8=sQuery(id+"F0.wireOp",EDGE,"E1.top");var subQ9=sQuery(id+"F0.wireOp",EDGE,"E1.left");var subQ10=sQuery(id+"F0.wireOp",EDGE,"E23.filletArc");var subQ11=sQuery(id+"F0.wireOp",EDGE,"E24.filletArc");Q0=makeQuery(id+"F2.boolean.opBoolean","SPLIT",FACE,{"disambiguationData":[TD([makeQuery(id+"F1.opExtrude","SWEPT_FACE",FACE,{"disambiguationData":[OSD([subQ6])]})])],"derivedFrom":makeQuery(id+"F1.opExtrude","CAP_FACE",FACE,{"disambiguationData":[OSD([subQ6,subQ8,subQ9,subQ7,subQ4,subQ3,subQ2,subQ1,subQ0,subQ5,subQ10,subQ11])],"isStart":true})});}
            var sketch = newSketch(context, id + "F16", { "sketchPlane" : qUnion([Q0])});
            skArc(sketch, "E79.0", {"start": v(-80, 90) * mm, "mid": v(-87.07, 87.07) * mm, "end": v(-90, 80) * mm});
            skLineSegment(sketch, "E79.1", {"start": v(-80, 90) * mm, "end": v(80, 90) * mm});
            skArc(sketch, "E79.2", {"start": v(90, 80) * mm, "mid": v(87.07, 87.07) * mm, "end": v(80, 90) * mm});
            skLineSegment(sketch, "E79.3", {"start": v(90, -80) * mm, "end": v(90, 80) * mm});
            skArc(sketch, "E79.4", {"start": v(80, -90) * mm, "mid": v(87.07, -87.07) * mm, "end": v(90, -80) * mm});
            skLineSegment(sketch, "E79.5", {"start": v(-80, -90) * mm, "end": v(80, -90) * mm});
            skArc(sketch, "E79.6", {"start": v(-90, -80) * mm, "mid": v(-87.07, -87.07) * mm, "end": v(-80, -90) * mm});
            skCircle(sketch, "E79.7", {"center": v(-60, -60) * mm, "radius": 4 * mm});
            skCircle(sketch, "E79.8", {"center": v(60, -60) * mm, "radius": 4 * mm});
            skCircle(sketch, "E79.9", {"center": v(60, 60) * mm, "radius": 4 * mm});
            skCircle(sketch, "E79.10", {"center": v(-60, 60) * mm, "radius": 4 * mm});
            skLineSegment(sketch, "E79.11", {"start": v(-60, 38.83) * mm, "end": v(-60, -38.83) * mm});
            skArc(sketch, "E79.12", {"start": v(-54.26, 47.88) * mm, "mid": v(-58.44, 44.2) * mm, "end": v(-60, 38.83) * mm});
            skArc(sketch, "E79.13", {"start": v(54.26, 47.88) * mm, "mid": v(0, 60) * mm, "end": v(-54.26, 47.88) * mm});
            skArc(sketch, "E79.14", {"start": v(60, 38.83) * mm, "mid": v(58.44, 44.2) * mm, "end": v(54.26, 47.88) * mm});
            skLineSegment(sketch, "E79.15", {"start": v(60, 38.83) * mm, "end": v(60, -38.83) * mm});
            skArc(sketch, "E79.16", {"start": v(54.26, -47.88) * mm, "mid": v(58.44, -44.2) * mm, "end": v(60, -38.83) * mm});
            skArc(sketch, "E79.17", {"start": v(-54.26, -47.88) * mm, "mid": v(0, -60) * mm, "end": v(54.26, -47.88) * mm});
            skArc(sketch, "E79.18", {"start": v(-60, -38.83) * mm, "mid": v(-58.44, -44.2) * mm, "end": v(-54.26, -47.88) * mm});
            skLineSegment(sketch, "E79.19", {"start": v(-90, -80) * mm, "end": v(-90, 80) * mm});
            skSolve(sketch);
        }
        {
            var Q0;
            Q0=qCreatedBy(makeId("Top.planeOp"),FACE);
            var sketch = newSketch(context, id + "F17", { "sketchPlane" : qUnion([Q0])});
            skLineSegment(sketch, "E80", {"start": v(-16.69, 108) * mm, "end": v(-16.69, 119) * mm});
            skLineSegment(sketch, "E81", {"start": v(11.19, 119) * mm, "end": v(11.19, 108) * mm});
            skLineSegment(sketch, "E82", {"start": v(11.19, 108) * mm, "end": v(28.9, 90.3) * mm});
            skArc(sketch, "E83", {"start": v(11.19, 119) * mm, "mid": v(-2.75, 128.45) * mm, "end": v(-16.69, 119) * mm});
            skLineSegment(sketch, "E84", {"start": v(-16.69, 108) * mm, "end": v(-30.3, 90.3) * mm});
            skCircle(sketch, "E85", {"center": v(-2.75, 113.45) * mm, "radius": 6 * mm});
            skLineSegment(sketch, "E86", {"start": v(-2.75, 113.45) * mm, "end": v(-2.75, 58.8) * mm, "construction": true});
            skLineSegment(sketch, "E87.MirrorCS", {"start": v(-2.75, -113.45) * mm, "end": v(-2.75, -58.8) * mm, "construction": true});
            skCircle(sketch, "E88.MirrorC", {"center": v(-2.75, -113.45) * mm, "radius": 6 * mm});
            skLineSegment(sketch, "E89.MirrorCS", {"start": v(-16.69, -108) * mm, "end": v(-30.3, -90.3) * mm});
            skLineSegment(sketch, "E90.MirrorCS", {"start": v(11.19, -108) * mm, "end": v(28.9, -90.3) * mm});
            skLineSegment(sketch, "E91.MirrorCS", {"start": v(11.19, -119) * mm, "end": v(11.19, -108) * mm});
            skArc(sketch, "E92.MirrorCS", {"start": v(11.19, -119) * mm, "mid": v(-2.75, -128.45) * mm, "end": v(-16.69, -119) * mm});
            skLineSegment(sketch, "E93.MirrorCS", {"start": v(-16.69, -108) * mm, "end": v(-16.69, -119) * mm});
            skLineSegment(sketch, "E94", {"start": v(-90.47, 0) * mm, "end": v(90.38, 0) * mm, "construction": true});
            skSolve(sketch);
        }
        {
            var Q0;
            Q0 = qSketchRegion(id + "F17", true);
            var Q1;
            Q1 = qSketchRegion(id + "F16", true);
            var Q2;
            Q2=makeQuery(id+"F2.opExtrude","CAP_FACE",FACE,{"disambiguationData":[OSD([sQuery(id+"F0.wireOp",EDGE,"E12"),sQuery(id+"F0.wireOp",EDGE,"E13"),sQuery(id+"F0.wireOp",EDGE,"E14"),sQuery(id+"F0.wireOp",EDGE,"E15"),sQuery(id+"F0.wireOp",EDGE,"E17.filletArc"),sQuery(id+"F0.wireOp",EDGE,"E18.filletArc"),sQuery(id+"F0.wireOp",EDGE,"E19.filletArc"),sQuery(id+"F0.wireOp",EDGE,"E20.filletArc"),sQuery(id+"F0.wireOp",EDGE,"E25.0"),sQuery(id+"F0.wireOp",EDGE,"E25.1"),sQuery(id+"F0.wireOp",EDGE,"E25.2"),sQuery(id+"F0.wireOp",EDGE,"E25.3"),sQuery(id+"F0.wireOp",EDGE,"E25.4"),sQuery(id+"F0.wireOp",EDGE,"E25.5"),sQuery(id+"F0.wireOp",EDGE,"E25.6"),sQuery(id+"F0.wireOp",EDGE,"E25.7")])],"isStart":false});
            extrude(context, id + "F18", {"entities" : qUnion([Q0, Q1]), "endBound" : BoundingType.UP_TO_SURFACE, "endBoundEntityFace" : qUnion([Q2]), "depth" : 25 * mm});
        }
    });
